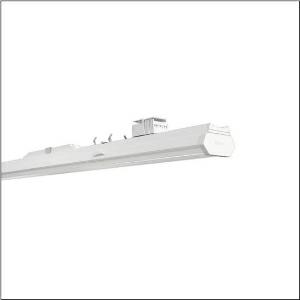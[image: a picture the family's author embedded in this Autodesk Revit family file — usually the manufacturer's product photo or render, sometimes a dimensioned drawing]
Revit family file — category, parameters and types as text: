
# Revit family: licross_11_protected_ho_51td1bdn4e5m3c
name_source: partatom
category: Lighting Fixtures
units: mm (PartAtom-declared; Revit-internal decimal feet)

## family parameters
Cut with Voids When Loaded = No
Host = Face
Light Source = No
Part Type = Normal
Room Calculation Point = No
Round Connector Dimension = Use Diameter
Shared = No

## types (1)
- --- (1 x LED, 920 lm, 7.4 W, 4000K)
    Apparent Load = 7 VA
    CIE Flux Codes = 54 82 95 97 100
    Color Rendering = 80
    Color Temperature = 4000K
    Default Elevation = 1800 mm
    Description = Licross 11 Protected HO, luminaire insert, of sheet steel, galvanised, coil coated, white, length: 1.500mm, width: 90mm, height: 101mm, LED rated luminous flux: 14.500lm, light colour: 840, SDCM (Standard Deviation of Colour Matching)MacAdam ≤ 2 SDCM (initial), control gear: DALI 2 (for two DALI lines), with plug, 6-pole, with phase selection, for trunking rail, 14-core, mains connection: 220..240V, AC, 50/60Hz, rated input power: 91W, for trunking rail, 14-core, internal wiring halogen-free, for emergency light function, converter,control gear: single battery element, battery: LiFePO4, 9Ah, primary optical cover: cover, of PMMA, light emission: direct distribution, primary light characteristic: symmetric, protection rating (complete): IP54, insulation class (complete): insulation class I (protective earthing), certification: CE, UKCA, protection symbol: D if used in an environment with non-conductive dust loads with corresponding accessories, impact resistance: IK06, permissible ambient temperature for indoor applications: +5..+30°C, standard: EN 60598-2-22, LABS conformity tested according to VDMA 24364:2018-05, reducing of maximum allowable ambient temperature of 5°C with ceiling mounting, corresponds to IFS (International Featured Standards) requirements for safety and quality in the food industry, The light source and the operating device comply with the requirements of the Ecodesign Regulation (EU) 2019/2020 and are replaceable in accordance with this regulation, packaging unit: 1 piece
    Height = 92 mm
    Lamp = 1 x LED
    Lamp Light Flux = 920 lm
    Lamp Power = 7.4 W
    Lamp count = 1
    Length = 1500 mm
    Luminous efficacy = 124 lm/W
    Manufacturer = Siteco
    ModVariant = No
    Model = 51TD1BDN4E5M3C
    Mounting Place = Ceiling
    Mounting Type = Pendant
    Number of Poles = 1
    OnlyDefault = Yes
    Power Factor = 1
    Product Name = Licross 11 Protected HO
    Product group = luminaire insert | ceiling pendant
    ProductGroupID = 901
    Protection Class = Protection class I
    Protection Degree = IP 54
    RLX_Detail_Level = 1
    RLX_Emergency_Light_Flux = 0 lm
    RLX_Emergency_Type = 0
    RLX_Emergency_Type_DB = No
    RlxData = <blob elided: 25041 chars, md5=1e9cc308>
    Socket = socket
    Standby Power = 0 W
    System Light Flux = 920 lm
    System Power = 7 W
    Type Comments = : emergency light operation: 3 h
    Type Image = l_1256145.jpg
    URL = http://relux.com
    VarID = @adj_095139
    Voltage = 0 V
    Weight = 0.00 kg
    Width = 88 mm

## geometry (parser evidence)
native form markers: Blend x4, Sweep x10
no freeform markers — native parametric forms only
